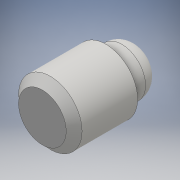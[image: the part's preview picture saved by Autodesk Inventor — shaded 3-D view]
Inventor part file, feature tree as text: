
AUTODESK INVENTOR PART (.ipt)
format: ipt  version: 2016 (Build 200138000, 138)  size: 131,072 bytes
history: native  units: mm
features: extrude x2, sketch x2, fillet x1, chamfer x1
ambient origin geometry x8: Origin, YZ Plane, XZ Plane, XY Plane, X Axis, Y Axis, Z Axis, Center Point
bodies: Solid1 (feature_tree)
feature tree (6):
  extrude  "Extrusion1"  Depth=2.0mm TaperAngle=0.0deg
  extrude  "Extrusion2"  Depth=4.0mm TaperAngle=0.0deg
  fillet  "Fillet1"  Radius=1.0mm
  chamfer  "Chamfer1"  Distance=0.5mm Angle=45.0deg
  sketch  "Sketch1"  dims[d0=3.0mm d1=2.0mm d2=0.0mm]
  sketch  "Sketch2"  dims[d3=4.0mm d4=4.0mm d5=0.0mm d6=1.0mm d7=0.5mm d8=2.0mm d9=45.0deg]
